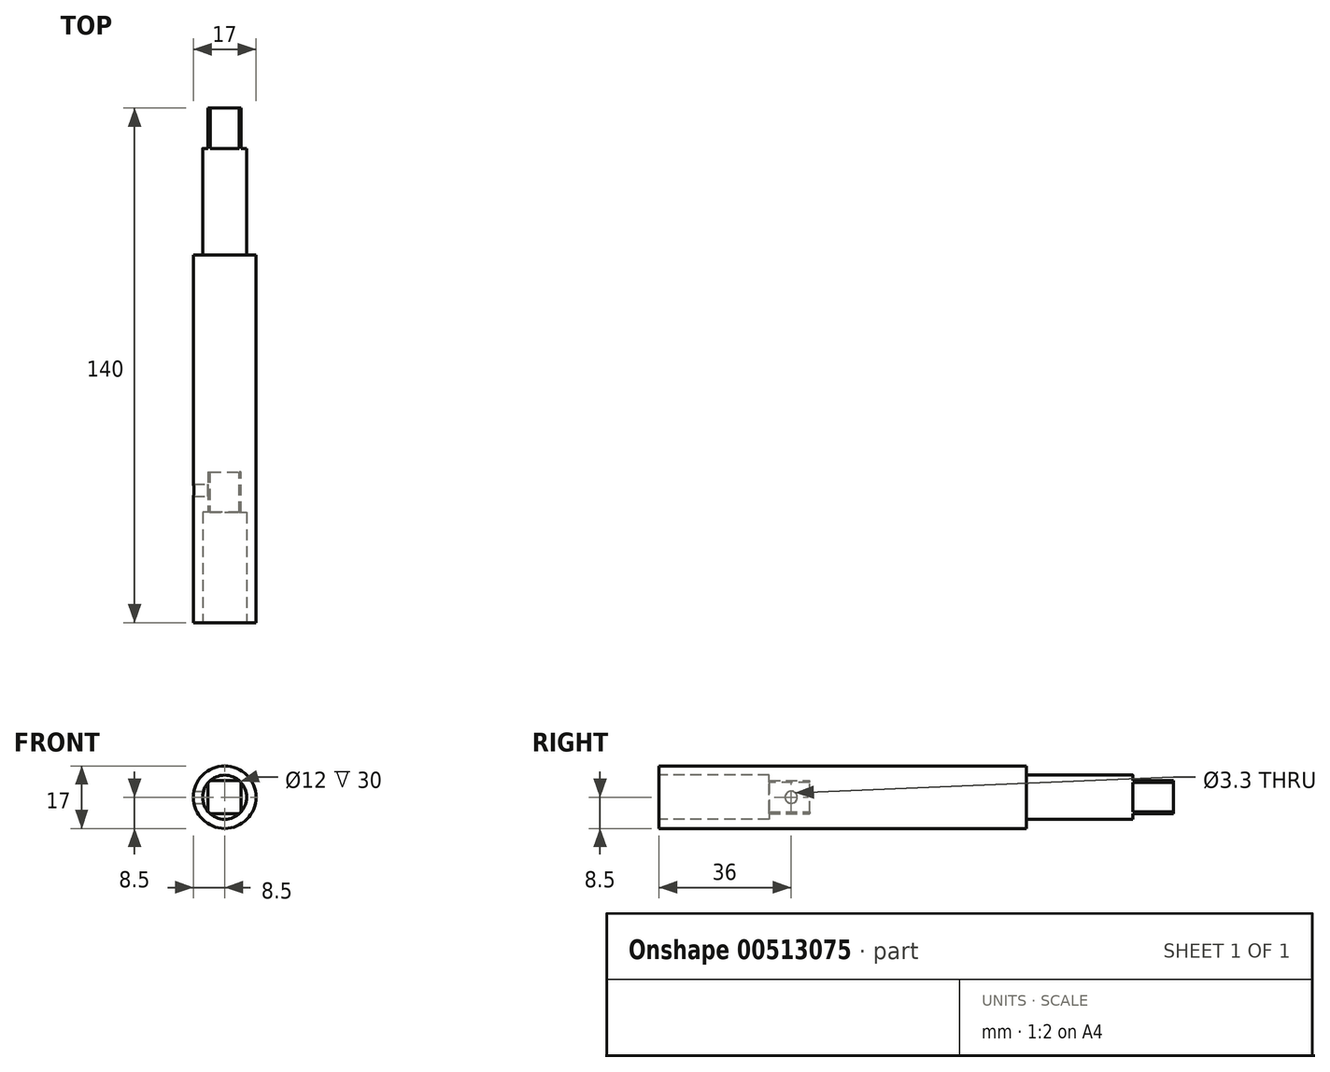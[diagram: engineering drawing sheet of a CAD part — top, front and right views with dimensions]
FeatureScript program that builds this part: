
annotation { "Feature Type Name" : "Feature", "Feature Type Description" : "" }
export const myFeature = defineFeature(function(context is Context, id is Id, definition is map)
    precondition{}
    {
        {
            var Q0;
            Q0=qCreatedBy(makeId("Front.planeOp"),FACE);
            var sketch = newSketch(context, id + "F0", { "sketchPlane" : qUnion([Q0])});
            skCircle(sketch, "E0", {"center": v(0, 0) * mm, "radius": 8.5 * mm});
            skSolve(sketch);
        }
        {
            var Q0;
            Q0=qSketchRegion(id+"F0",true);
            extrude(context, id + "F1", {"entities" : qUnion([Q0]), "depth" : 140 * mm});
        }
        {
            var Q0;
            Q0=makeQuery(id+"F1.opExtrude","CAP_FACE",FACE,{"disambiguationData":[OSD([sQuery(id+"F0.wireOp",EDGE,"E0")])],"isStart":false});
            var sketch = newSketch(context, id + "F2", { "sketchPlane" : qUnion([Q0])});
            skCircle(sketch, "E1", {"center": v(0, 0) * mm, "radius": 6 * mm});
            skSolve(sketch);
        }
        {
            var Q0;
            Q0=qSketchRegion(id+"F2",true);
            extrude(context, id + "F3", {"entities" : qUnion([Q0]), "operationType" : NewBodyOperationType.REMOVE, "oppositeDirection" : true, "depth" : 30 * mm});
        }
        {
            var Q0;
            Q0=makeQuery(id+"F3.boolean.opBoolean","COPY",FACE,{"derivedFrom":makeQuery(id+"F3.opExtrude","CAP_FACE",FACE,{"disambiguationData":[OSD([sQuery(id+"F2.wireOp",EDGE,"E1")])],"isStart":false})});
            var sketch = newSketch(context, id + "F4", { "sketchPlane" : qUnion([Q0])});
            skLineSegment(sketch, "E2.bottom", {"start": v(-4.5, -4.5) * mm, "end": v(4.5, -4.5) * mm});
            skLineSegment(sketch, "E2.top", {"start": v(-4.5, 4.5) * mm, "end": v(4.5, 4.5) * mm});
            skLineSegment(sketch, "E2.left", {"start": v(-4.5, -4.5) * mm, "end": v(-4.5, 4.5) * mm});
            skLineSegment(sketch, "E2.right", {"start": v(4.5, -4.5) * mm, "end": v(4.5, 4.5) * mm});
            skPoint(sketch, "E2.middle", {"position": v(0, 0) * mm});
            skSolve(sketch);
        }
        {
            var Q0;
            Q0=qSketchRegion(id+"F4",true);
            extrude(context, id + "F5", {"entities" : qUnion([Q0]), "operationType" : NewBodyOperationType.REMOVE, "oppositeDirection" : true, "depth" : 11 * mm});
        }
        {
            var Q0;
            Q0=makeQuery(id+"F5.boolean.opBoolean","COPY",EDGE,{"derivedFrom":makeQuery(id+"F5.opExtrude","SWEPT_EDGE",EDGE,{"disambiguationData":[OSD([sQuery(id+"F4.wireOp",EDGE,"E2.bottom"),sQuery(id+"F4.wireOp",EDGE,"E2.left")])]})});
            chamfer(context, id + "F6", {"entities" : qUnion([Q0]), "width" : .5 * mm, "tangentPropagation" : true});
        }
        {
            var Q0;
            Q0=makeQuery(id+"F5.boolean.opBoolean","COPY",EDGE,{"derivedFrom":makeQuery(id+"F5.opExtrude","SWEPT_EDGE",EDGE,{"disambiguationData":[OSD([sQuery(id+"F4.wireOp",EDGE,"E2.bottom"),sQuery(id+"F4.wireOp",EDGE,"E2.right")])]})});
            chamfer(context, id + "F7", {"entities" : qUnion([Q0]), "width" : .5 * mm, "tangentPropagation" : true});
        }
        {
            var Q0;
            Q0=makeQuery(id+"F5.boolean.opBoolean","COPY",EDGE,{"derivedFrom":makeQuery(id+"F5.opExtrude","SWEPT_EDGE",EDGE,{"disambiguationData":[OSD([sQuery(id+"F4.wireOp",EDGE,"E2.top"),sQuery(id+"F4.wireOp",EDGE,"E2.right")])]})});
            var Q1;
            Q1=makeQuery(id+"F5.boolean.opBoolean","COPY",EDGE,{"derivedFrom":makeQuery(id+"F5.opExtrude","SWEPT_EDGE",EDGE,{"disambiguationData":[OSD([sQuery(id+"F4.wireOp",EDGE,"E2.top"),sQuery(id+"F4.wireOp",EDGE,"E2.left")])]})});
            chamfer(context, id + "F8", {"entities" : qUnion([Q0, Q1]), "width" : .5 * mm, "tangentPropagation" : true});
        }
        {
            var Q0;
            Q0=makeQuery(id+"F5.boolean.opBoolean","COPY",FACE,{"derivedFrom":makeQuery(id+"F5.opExtrude","SWEPT_FACE",FACE,{"disambiguationData":[OSD([sQuery(id+"F4.wireOp",EDGE,"E2.left")])]})});
            var sketch = newSketch(context, id + "F9", { "sketchPlane" : qUnion([Q0])});
            skCircle(sketch, "E3", {"center": v(-104, 0) * mm, "radius": 1.65 * mm});
            skSolve(sketch);
        }
        {
            var Q0;
            Q0=qSketchRegion(id+"F9",true);
            extrude(context, id + "F10", {"entities" : qUnion([Q0]), "operationType" : NewBodyOperationType.REMOVE, "oppositeDirection" : true, "depth" : 25 * mm});
        }
        {
            var Q0;
            Q0=makeQuery(id+"F1.opExtrude","CAP_FACE",FACE,{"disambiguationData":[OSD([sQuery(id+"F0.wireOp",EDGE,"E0")])],"isStart":true});
            var sketch = newSketch(context, id + "F11", { "sketchPlane" : qUnion([Q0])});
            skCircle(sketch, "E4", {"center": v(0, 0) * mm, "radius": 6 * mm});
            skSolve(sketch);
        }
        {
            var Q0;
            Q0=makeQuery(id+"F11.imprint","IMPRINT",FACE,{"disambiguationData":[TD([[makeQuery(id+"F11.imprint","IMPRINT",EDGE,{"derivedFrom":sQuery(id+"F11.wireOp",EDGE,"E4")}),-1.0]])]});
            extrude(context, id + "F12", {"entities" : qUnion([Q0]), "operationType" : NewBodyOperationType.REMOVE, "oppositeDirection" : true, "depth" : 40 * mm});
        }
        {
            var Q0;
            Q0=makeQuery(id+"F1.opExtrude","CAP_FACE",FACE,{"disambiguationData":[OSD([sQuery(id+"F0.wireOp",EDGE,"E0")])],"isStart":true});
            var sketch = newSketch(context, id + "F13", { "sketchPlane" : qUnion([Q0])});
            skLineSegment(sketch, "E5.bottom", {"start": v(-4.5, -4.5) * mm, "end": v(4.5, -4.5) * mm});
            skLineSegment(sketch, "E5.top", {"start": v(-4.5, 4.5) * mm, "end": v(4.5, 4.5) * mm});
            skLineSegment(sketch, "E5.left", {"start": v(-4.5, -4.5) * mm, "end": v(-4.5, 4.5) * mm});
            skLineSegment(sketch, "E5.right", {"start": v(4.5, -4.5) * mm, "end": v(4.5, 4.5) * mm});
            skPoint(sketch, "E5.middle", {"position": v(0, 0) * mm});
            skSolve(sketch);
        }
        {
            var Q0;
            {var subQ0=sQuery(id+"F13.wireOp",EDGE,"E5.top");var subQ1=makeQuery(id+"F12.boolean.opBoolean","COPY",EDGE,{"derivedFrom":makeQuery(id+"F12.opExtrude","CAP_EDGE",EDGE,{"disambiguationData":[OSD([sQuery(id+"F11.wireOp",EDGE,"E4")])],"isStart":true})});var subQ2=makeQuery(id+"F13.imprint","INTERSECT",VERTEX,{"disambiguationData":[OD(0.0)],"derivedFrom":[subQ1,subQ0]});Q0=makeQuery(id+"F13.imprint","IMPRINT",FACE,{"disambiguationData":[TD([[makeQuery(id+"F13.imprint","IMPRINT",EDGE,{"disambiguationData":[TD([[subQ2,-1.0]])],"derivedFrom":subQ0}),1.0]])]});}
            var Q1;
            {var subQ0=sQuery(id+"F13.wireOp",EDGE,"E5.right");var subQ1=makeQuery(id+"F12.boolean.opBoolean","COPY",EDGE,{"derivedFrom":makeQuery(id+"F12.opExtrude","CAP_EDGE",EDGE,{"disambiguationData":[OSD([sQuery(id+"F11.wireOp",EDGE,"E4")])],"isStart":true})});var subQ2=makeQuery(id+"F13.imprint","INTERSECT",VERTEX,{"disambiguationData":[OD(0.0)],"derivedFrom":[subQ1,subQ0]});Q1=makeQuery(id+"F13.imprint","IMPRINT",FACE,{"disambiguationData":[TD([[makeQuery(id+"F13.imprint","IMPRINT",EDGE,{"disambiguationData":[TD([[subQ2,-1.0]])],"derivedFrom":subQ0}),-1.0]])]});}
            var Q2;
            {var subQ0=sQuery(id+"F13.wireOp",EDGE,"E5.bottom");var subQ1=makeQuery(id+"F12.boolean.opBoolean","COPY",EDGE,{"derivedFrom":makeQuery(id+"F12.opExtrude","CAP_EDGE",EDGE,{"disambiguationData":[OSD([sQuery(id+"F11.wireOp",EDGE,"E4")])],"isStart":true})});var subQ2=makeQuery(id+"F13.imprint","INTERSECT",VERTEX,{"disambiguationData":[OD(0.0)],"derivedFrom":[subQ1,subQ0]});Q2=makeQuery(id+"F13.imprint","IMPRINT",FACE,{"disambiguationData":[TD([[makeQuery(id+"F13.imprint","IMPRINT",EDGE,{"disambiguationData":[TD([[subQ2,-1.0]])],"derivedFrom":subQ0}),-1.0]])]});}
            var Q3;
            {var subQ0=sQuery(id+"F13.wireOp",EDGE,"E5.left");var subQ1=makeQuery(id+"F12.boolean.opBoolean","COPY",EDGE,{"derivedFrom":makeQuery(id+"F12.opExtrude","CAP_EDGE",EDGE,{"disambiguationData":[OSD([sQuery(id+"F11.wireOp",EDGE,"E4")])],"isStart":true})});var subQ2=makeQuery(id+"F13.imprint","INTERSECT",VERTEX,{"disambiguationData":[OD(0.0)],"derivedFrom":[subQ1,subQ0]});Q3=makeQuery(id+"F13.imprint","IMPRINT",FACE,{"disambiguationData":[TD([[makeQuery(id+"F13.imprint","IMPRINT",EDGE,{"disambiguationData":[TD([[subQ2,-1.0]])],"derivedFrom":subQ0}),1.0]])]});}
            extrude(context, id + "F14", {"entities" : qUnion([Q0, Q1, Q2, Q3]), "operationType" : NewBodyOperationType.REMOVE, "oppositeDirection" : true, "depth" : 11 * mm});
        }
    });
